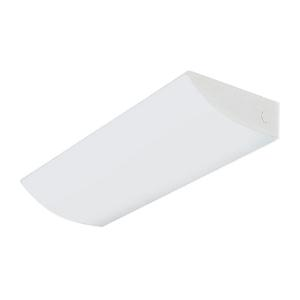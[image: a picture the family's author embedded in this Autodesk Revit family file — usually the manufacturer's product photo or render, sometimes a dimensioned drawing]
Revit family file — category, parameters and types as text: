
# Revit family: 3f_filippi_-_mira_par_ind_3f_filippi_-_1959_-_mira_par_led_4x12w_ind_l675
name_source: partatom
category: Lighting Fixtures
units: mm (PartAtom-declared; Revit-internal decimal feet)

## family parameters
Cut with Voids When Loaded = No
Host = Face
Light Source = No
Part Type = Normal
Room Calculation Point = No
Round Connector Dimension = Use Diameter
Shared = No

## types (1)
- 3F Filippi - Mira Par Ind (1 x LED, 6840 lm, 56 W, 4000 K)
    Apparent Load = 56 VA
    Approval mark = ENEC
    CIE Flux Codes = - - - 0 100
    Color Rendering = 80
    Color Temperature = 4000 K
    Control Gear = Electronic ballast
    Default Elevation = 1800 mm
    Description = ILLUMINOTECHNICAL
Luminous efficiency 100% (DLOR 0%, ULOR 100%).
Initial luminous flux of the luminaire 6840 lm.
Asymmetric indirect distribution.
Beam angle: 77° - 106°.
Luminous efficacy 122 lm/W.
Lifetime (L93/B10): 30000 h. (tq+25°C)
Lifetime (L90/B10): 50000 h. (tq+25°C)
Lifetime (L85/B10): 80000 h. (tq+25°C)
Lifetime (L80/B10): 100000 h. (tq+25°C)
Sudden decreased luminous flux after 50000 hours: 0% (C0).
Photobiological safety in compliance with IEC/TR 62778: RG0 risk exempt, (IEC 62471).
In compliance with IEC/EN 62722-2-1 - IEC/EN 62717 standards.

SOURCE
4 linear LED modules 12W/840.
Energy efficiency class (UE 2019/2020 - UE 2019/2015): D.
CIE 13.3 Colour rendering index: CRI >80 (R9 <50%).
IES TM-30 Fidelity Index: Rf = 84 Rg = 95.
CCT nominal colour temperature 4000 K.
Colour initial tolerance (MacAdam): SDCM 3.

MECHANICAL
Housing in white painted steel.
Asymmetric flow recuperator, high efficiency, in specular aluminium with superficial titanium-magnesium treatment.
Upper diffuser in transparent polycarbonate, self-extinguishing V2, UV stabilised.
Luminaire with limited surface temperature. - D - (EN 60598-2-24)
Dimensions: 675x230 mm, height 80 mm. Weight 2.48 kg.
IP40 protection degree.
Glow-wire test resistance 850°C.

ELECTRICAL
Halogen Free electronic wiring 230V-50/60Hz, power factor 0.95, THD <25%, constant output current, SELV, class I, 1 driver.
Power of the luminaire 56 W.
CE - IEC 60598-1 - EN 60598-1.
SAFE FLICKER: PstLM=<1 and SVM=<0.4 (IEC TR 61547-1 and IEC TR 63158), to ensure a more comfortable and safe light.
Luminaire compliant with EN 60598-2-22 for power supply from a centralised emergency system CPSS (Central Power Supply System), not incorporated in the luminaire - high risk areas excluded. The default power and flux are 100% in AC and 100% in DC.
Ambient temperature from 0°C to +25°C.
Temperature class T6 max 85°C.
Relative humidity UR: <85%.

INSTALLATION
Wall.
All accessories dedicated to this product are available on the Catalog and on our website www.3F-Filippi.com.

APPLICATIONS
Environments where a comfortable light is required. Luminaire for wall mounting, with an essential and modern design. Suitable for offices, conference rooms, managerial offices.

WARNING
Luminaire designed for disposal/recycling at end-of-life.
Replaceable (LED only) light source by a professional. Replaceable control gear by a professional.
    Height = 80 mm  [stored 0.262467 ft]
    Lamp = 1 x LED
    Lamp Light Flux = 6840 lm
    Lamp Power = 56 W
    Lamp count = 1
    Length = 675 mm
    Lifetime = 50000 h
    Luminous efficacy = 122 lm/W
    Manufacturer = 3F Filippi
    ModVariant = No
    Model = 3F Filippi - 1959 - MIRA PAR LED 4x12W IND L675
    Mounting Place = Wall
    Mounting Type = Surface mounted
    Number of Poles = 1
    OnlyDefault = Yes
    Power Factor = 1
    Product Name = 3F Filippi - Mira Par Ind
    Product group = wall-mounted luminaire
    ProductGroupID = 20
    Protection Class = Protection class I
    Protection Degree = IP 40
    RLX_Detail_Level = 1
    RLX_Emergency_Light_Flux = 0 lm
    RLX_Emergency_Type = 0
    RLX_Emergency_Type_DB = No
    RlxData = <blob elided: 32277 chars, md5=0acda0bb>
    Socket = socket
    Standby Power = 0 W
    System Light Flux = 6840 lm
    System Power = 56 W
    Type Comments = Product without accessories
    Type Image = 3ffilippi_mira_par_ind.jpg
    URL = http://relux.com
    VarID = ---
    Voltage = 0 V
    Weight = 0.00 kg
    Width = 230 mm

note: [stored X ft] marks values corroborated as IEEE doubles in the binary element streams (Revit-internal decimal feet)

## geometry (parser evidence)
native form markers: Blend x4, Sweep x10
no freeform markers — native parametric forms only
